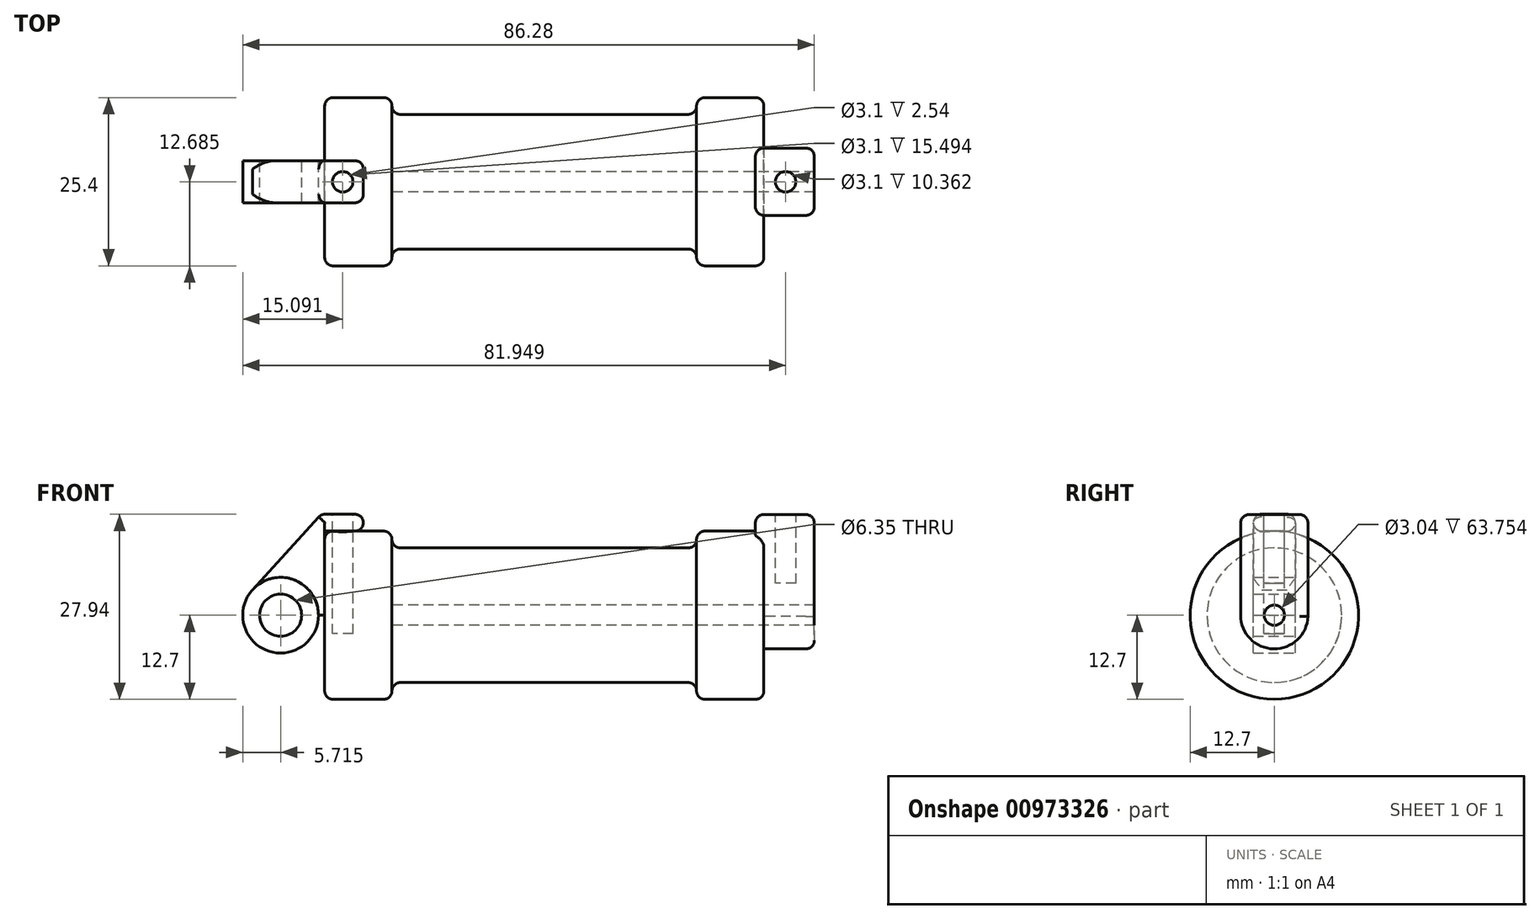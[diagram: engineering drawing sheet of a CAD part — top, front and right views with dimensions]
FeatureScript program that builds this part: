
annotation { "Feature Type Name" : "Feature", "Feature Type Description" : "" }
export const myFeature = defineFeature(function(context is Context, id is Id, definition is map)
    precondition{}
    {
        {
            var Q0;
            Q0=qCreatedBy(makeId("Front.planeOp"),FACE);
            var sketch = newSketch(context, id + "F0", { "sketchPlane" : qUnion([Q0])});
            skLineSegment(sketch, "E0", {"start": v(0, 0) * mm, "end": v(0, 12.7) * mm});
            skLineSegment(sketch, "E1", {"start": v(0, 12.7) * mm, "end": v(10.16, 12.7) * mm});
            skLineSegment(sketch, "E2", {"start": v(10.16, 12.7) * mm, "end": v(10.16, 10.16) * mm});
            skLineSegment(sketch, "E3", {"start": v(10.16, 10.16) * mm, "end": v(56.13, 10.16) * mm});
            skLineSegment(sketch, "E4", {"start": v(56.13, 10.16) * mm, "end": v(56.13, 12.7) * mm});
            skLineSegment(sketch, "E5", {"start": v(56.13, 12.7) * mm, "end": v(66.3, 12.7) * mm});
            skLineSegment(sketch, "E6", {"start": v(66.3, 12.7) * mm, "end": v(66.3, 0) * mm});
            skLineSegment(sketch, "E7", {"start": v(66.3, 0) * mm, "end": v(0, 0) * mm});
            skLineSegment(sketch, "E8", {"start": v(5.84, 15.24) * mm, "end": v(-0.5, 15.24) * mm});
            skLineSegment(sketch, "E9", {"start": v(-0.5, 15.24) * mm, "end": v(-10.88, 3.85) * mm});
            skLineSegment(sketch, "E10", {"start": v(0, 0) * mm, "end": v(-6.65, 0) * mm});
            skCircle(sketch, "E11", {"center": v(-6.65, 0) * mm, "radius": 5.72 * mm});
            skCircle(sketch, "E12", {"center": v(-6.65, 0) * mm, "radius": 3.18 * mm});
            skLineSegment(sketch, "E13", {"start": v(5.84, 15.24) * mm, "end": v(5.84, -9.4) * mm});
            skLineSegment(sketch, "E14", {"start": v(5.84, -9.4) * mm, "end": v(-8.18, -5.5) * mm});
            skSolve(sketch);
        }
        {
            var Q0;
            {var subQ0=sQuery(id+"F0.wireOp",EDGE,"E0");Q0=makeQuery(id+"F0.imprint","IMPRINT",FACE,{"disambiguationData":[TD([[makeQuery(id+"F0.imprint","IMPRINT",EDGE,{"derivedFrom":subQ0}),-1.0]])]});}
            var Q1;
            {var subQ0=sQuery(id+"F0.wireOp",EDGE,"E2");Q1=makeQuery(id+"F0.imprint","IMPRINT",FACE,{"disambiguationData":[TD([[makeQuery(id+"F0.imprint","IMPRINT",EDGE,{"derivedFrom":subQ0}),-1.0]])]});}
            var Q2;
            Q2=sQuery(id+"F0.wireOp",EDGE,"E10");
            revolve(context, id + "F1", {"surfaceOperationType" : NewSurfaceOperationType.NEW, "entities" : qUnion([Q0, Q1]), "axis" : qUnion([Q2]), "revolveType" : RevolveType.FULL});
        }
        {
            var Q0;
            {var subQ5=sQuery(id+"F0.wireOp",EDGE,"E12");Q0=makeQuery(id+"F0.imprint","IMPRINT",FACE,{"disambiguationData":[TD([[makeQuery(id+"F0.imprint","IMPRINT",EDGE,{"derivedFrom":subQ5}),-1.0]])]});}
            extrude(context, id + "F2", {"entities" : qUnion([Q0]), "endBound" : BoundingType.SYMMETRIC, "depth" : 6.35 * mm, "offsetDistance" : 25.4 * mm});
        }
        {
            var Q0;
            {var subQ1=sQuery(id+"F0.wireOp",EDGE,"E0");Q0=makeQuery(id+"F0.imprint","IMPRINT",FACE,{"disambiguationData":[TD([[makeQuery(id+"F0.imprint","IMPRINT",EDGE,{"derivedFrom":subQ1}),1.0]])]});}
            extrude(context, id + "F3", {"entities" : qUnion([Q0]), "endBound" : BoundingType.SYMMETRIC, "depth" : 6.35 * mm, "offsetDistance" : 25.4 * mm});
        }
        {
            var Q0;
            Q0=makeQuery(id+"F1.opRevolve","SWEPT_FACE",FACE,{"disambiguationData":[OSD([sQuery(id+"F0.wireOp",EDGE,"E6")])]});
            var sketch = newSketch(context, id + "F4", { "sketchPlane" : qUnion([Q0])});
            skCircle(sketch, "E15", {"center": v(0, 0) * mm, "radius": 1.52 * mm});
            skCircle(sketch, "E16", {"center": v(0, 0) * mm, "radius": 5.08 * mm});
            skLineSegment(sketch, "E17", {"start": v(-5.08, -0.02) * mm, "end": v(-5.08, 15.19) * mm});
            skLineSegment(sketch, "E18", {"start": v(-5.08, 15.19) * mm, "end": v(5.08, 15.19) * mm});
            skLineSegment(sketch, "E19", {"start": v(5.08, 15.19) * mm, "end": v(5.08, -0.19) * mm});
            skSolve(sketch);
        }
        {
            var Q0;
            {var subQ0=sQuery(id+"F4.wireOp",EDGE,"E17");var subQ1=sQuery(id+"F4.wireOp",EDGE,"E16");var subQ2=makeQuery(id+"F4.imprint","INTERSECT",VERTEX,{"derivedFrom":[subQ1,subQ0]});Q0=makeQuery(id+"F4.imprint","IMPRINT",FACE,{"disambiguationData":[TD([[makeQuery(id+"F4.imprint","IMPRINT",EDGE,{"disambiguationData":[TD([[subQ2,1.0]])],"derivedFrom":subQ1}),-1.0]])]});}
            var Q1;
            Q1=makeQuery(id+"F4.imprint","IMPRINT",FACE,{"disambiguationData":[TD([[makeQuery(id+"F4.imprint","IMPRINT",EDGE,{"derivedFrom":sQuery(id+"F4.wireOp",EDGE,"E15")}),-1.0]])]});
            var Q2;
            {var subQ0=sQuery(id+"F4.wireOp",EDGE,"E18");Q2=makeQuery(id+"F4.imprint","IMPRINT",FACE,{"disambiguationData":[TD([[makeQuery(id+"F4.imprint","IMPRINT",EDGE,{"derivedFrom":subQ0}),-1.0]])]});}
            extrude(context, id + "F5", {"entities" : qUnion([Q0, Q1, Q2]), "operationType" : NewBodyOperationType.ADD, "depth" : 7.62 * mm, "offsetDistance" : 25.4 * mm});
        }
        {
            var Q0;
            Q0 = qSketchRegion(id + "F4", true);
            extrude(context, id + "F6", {"entities" : qUnion([Q0]), "operationType" : NewBodyOperationType.ADD, "oppositeDirection" : true, "depth" : 1.27 * mm, "offsetDistance" : 25.4 * mm});
        }
        {
            var Q0;
            Q0=makeQuery(id+"F5.boolean.opBoolean","SPLIT",FACE,{"disambiguationData":[TD([makeQuery(id+"F5.opExtrude","SWEPT_FACE",FACE,{"disambiguationData":[OSD([sQuery(id+"F4.wireOp",EDGE,"E15")])]})])],"derivedFrom":makeQuery(id+"F1.opRevolve","SWEPT_FACE",FACE,{"disambiguationData":[OSD([sQuery(id+"F0.wireOp",EDGE,"E6")])]})});
            var Q1;
            Q1=makeQuery(id+"F1.opRevolve","SWEPT_FACE",FACE,{"disambiguationData":[OSD([sQuery(id+"F0.wireOp",EDGE,"E2")])]});
            var Q2;
            Q2=makeQuery(id+"F1.opRevolve","SWEPT_BODY",BODY,{"disambiguationData":[OSD([sQuery(id+"F0.wireOp",EDGE,"E0"),sQuery(id+"F0.wireOp",EDGE,"E1"),sQuery(id+"F0.wireOp",EDGE,"E2"),sQuery(id+"F0.wireOp",EDGE,"E3"),sQuery(id+"F0.wireOp",EDGE,"E4"),sQuery(id+"F0.wireOp",EDGE,"E5"),sQuery(id+"F0.wireOp",EDGE,"E6"),sQuery(id+"F0.wireOp",EDGE,"E7")])]});
            extrude(context, id + "F7", {"entities" : qUnion([Q0]), "operationType" : NewBodyOperationType.ADD, "oppositeDirection" : true, "depth" : 60.32 * mm, "endBoundEntityFace" : qUnion([Q1]), "endBoundEntityBody" : qUnion([Q2]), "offsetDistance" : 25.4 * mm});
        }
        {
            var Q0;
            Q0=makeQuery(id+"F5.boolean.opBoolean","SPLIT",FACE,{"disambiguationData":[TD([makeQuery(id+"F5.opExtrude","SWEPT_FACE",FACE,{"disambiguationData":[OSD([sQuery(id+"F4.wireOp",EDGE,"E15")])]})])],"derivedFrom":makeQuery(id+"F1.opRevolve","SWEPT_FACE",FACE,{"disambiguationData":[OSD([sQuery(id+"F0.wireOp",EDGE,"E6")])]})});
            extrude(context, id + "F8", {"entities" : qUnion([Q0]), "operationType" : NewBodyOperationType.REMOVE, "oppositeDirection" : true, "depth" : 56.13 * mm, "offsetDistance" : 25.4 * mm});
        }
        {
            var Q0;
            Q0=makeQuery(id+"F3.opExtrude","SWEPT_FACE",FACE,{"disambiguationData":[OSD([sQuery(id+"F0.wireOp",EDGE,"E8")])]});
            var sketch = newSketch(context, id + "F9", { "sketchPlane" : qUnion([Q0])});
            skCircle(sketch, "E20", {"center": v(2.72, -0.01) * mm, "radius": 1.55 * mm});
            skCircle(sketch, "E21", {"center": v(69.58, -0.01) * mm, "radius": 1.55 * mm});
            skSolve(sketch);
        }
        {
            var Q0;
            Q0=makeQuery(id+"F9.imprint","IMPRINT",FACE,{"disambiguationData":[TD([[makeQuery(id+"F9.imprint","IMPRINT",EDGE,{"derivedFrom":sQuery(id+"F9.wireOp",EDGE,"E20")}),1.0]])]});
            var Q1;
            Q1=sQuery(id+"F9.wireOp",EDGE,"E20");
            extrude(context, id + "F10", {"entities" : qUnion([Q0]), "operationType" : NewBodyOperationType.REMOVE, "surfaceEntities" : qUnion([Q1]), "oppositeDirection" : true, "depth" : 18.03 * mm, "offsetDistance" : 25.4 * mm});
        }
        {
            var Q0;
            Q0=makeQuery(id+"F9.imprint","IMPRINT",FACE,{"disambiguationData":[TD([[makeQuery(id+"F9.imprint","IMPRINT",EDGE,{"derivedFrom":sQuery(id+"F9.wireOp",EDGE,"E21")}),1.0]])]});
            extrude(context, id + "F11", {"entities" : qUnion([Q0]), "operationType" : NewBodyOperationType.REMOVE, "oppositeDirection" : true, "depth" : 10.4 * mm, "offsetDistance" : 25.4 * mm});
        }
        {
            var Q0;
            Q0=makeQuery(id+"F1.opRevolve","SWEPT_EDGE",EDGE,{"disambiguationData":[OSD([sQuery(id+"F0.wireOp",EDGE,"E1"),sQuery(id+"F0.wireOp",EDGE,"E2")])]});
            var Q1;
            Q1=makeQuery(id+"F1.opRevolve","SWEPT_EDGE",EDGE,{"disambiguationData":[OSD([sQuery(id+"F0.wireOp",EDGE,"E0"),sQuery(id+"F0.wireOp",EDGE,"E1")])]});
            var Q2;
            Q2=makeQuery(id+"F1.opRevolve","SWEPT_EDGE",EDGE,{"disambiguationData":[OSD([sQuery(id+"F0.wireOp",EDGE,"E4"),sQuery(id+"F0.wireOp",EDGE,"E5")])]});
            var Q3;
            {var subQ0=sQuery(id+"F0.wireOp",EDGE,"E5");var subQ1=sQuery(id+"F0.wireOp",EDGE,"E6");Q3=makeQuery(id+"F5.boolean.opBoolean","SPLIT",EDGE,{"disambiguationData":[topologyDisambiguationEdgeConnected([makeQuery(id+"F1.opRevolve","SWEPT_FACE",FACE,{"disambiguationData":[OSD([subQ1])]})])],"derivedFrom":makeQuery(id+"F1.opRevolve","SWEPT_EDGE",EDGE,{"disambiguationData":[OSD([subQ0,subQ1])]})});}
            fillet(context, id + "F12", {"entities" : qUnion([Q0, Q1, Q2, Q3]), "radius" : 1.27 * mm, "tangentPropagation" : true, "allowEdgeOverflow" : false});
        }
        {
            var Q0;
            Q0=makeQuery(id+"F1.opRevolve","SWEPT_EDGE",EDGE,{"disambiguationData":[OSD([sQuery(id+"F0.wireOp",EDGE,"E2"),sQuery(id+"F0.wireOp",EDGE,"E3")])]});
            var Q1;
            Q1=makeQuery(id+"F1.opRevolve","SWEPT_EDGE",EDGE,{"disambiguationData":[OSD([sQuery(id+"F0.wireOp",EDGE,"E3"),sQuery(id+"F0.wireOp",EDGE,"E4")])]});
            fillet(context, id + "F13", {"entities" : qUnion([Q0, Q1]), "radius" : 1.27 * mm, "tangentPropagation" : true, "allowEdgeOverflow" : false});
        }
        {
            var Q0;
            Q0=makeQuery(id+"F3.opExtrude","CAP_EDGE",EDGE,{"disambiguationData":[OSD([sQuery(id+"F0.wireOp",EDGE,"E9")])],"isStart":false});
            var Q1;
            Q1=makeQuery(id+"F3.opExtrude","CAP_EDGE",EDGE,{"disambiguationData":[OSD([sQuery(id+"F0.wireOp",EDGE,"E9")])],"isStart":true});
            fillet(context, id + "F14", {"entities" : qUnion([Q0, Q1]), "radius" : 1.27 * mm, "tangentPropagation" : true, "allowEdgeOverflow" : false});
        }
        {
            var Q0;
            Q0=makeQuery(id+"F3.opExtrude","CAP_EDGE",EDGE,{"disambiguationData":[OSD([sQuery(id+"F0.wireOp",EDGE,"E8")])],"isStart":false});
            var Q1;
            Q1=makeQuery(id+"F3.opExtrude","SWEPT_EDGE",EDGE,{"disambiguationData":[OSD([sQuery(id+"F0.wireOp",EDGE,"E8"),sQuery(id+"F0.wireOp",EDGE,"E13")])]});
            var Q2;
            Q2=makeQuery(id+"F3.opExtrude","CAP_EDGE",EDGE,{"disambiguationData":[OSD([sQuery(id+"F0.wireOp",EDGE,"E1")])],"isStart":true});
            var Q3;
            Q3=makeQuery(id+"F3.opExtrude","SWEPT_EDGE",EDGE,{"disambiguationData":[OSD([sQuery(id+"F0.wireOp",EDGE,"E1"),sQuery(id+"F0.wireOp",EDGE,"E13")])]});
            var Q4;
            Q4=makeQuery(id+"F3.opExtrude","CAP_EDGE",EDGE,{"disambiguationData":[OSD([sQuery(id+"F0.wireOp",EDGE,"E13")])],"isStart":true});
            var Q5;
            Q5=makeQuery(id+"F3.opExtrude","CAP_EDGE",EDGE,{"disambiguationData":[OSD([sQuery(id+"F0.wireOp",EDGE,"E13")])],"isStart":false});
            var Q6;
            Q6=makeQuery(id+"F3.opExtrude","CAP_EDGE",EDGE,{"disambiguationData":[OSD([sQuery(id+"F0.wireOp",EDGE,"E1")])],"isStart":false});
            fillet(context, id + "F15", {"entities" : qUnion([Q0, Q1, Q2, Q3, Q4, Q5, Q6]), "radius" : 1.27 * mm, "tangentPropagation" : true, "allowEdgeOverflow" : false});
        }
        {
            var Q0;
            Q0=makeQuery(id+"F5.opExtrude","CAP_EDGE",EDGE,{"disambiguationData":[OSD([sQuery(id+"F4.wireOp",EDGE,"E17")])],"isStart":false});
            var Q1;
            Q1=makeQuery(id+"F5.opExtrude","CAP_EDGE",EDGE,{"disambiguationData":[OSD([sQuery(id+"F4.wireOp",EDGE,"E16")])],"isStart":false});
            var Q2;
            Q2=makeQuery(id+"F5.opExtrude","CAP_EDGE",EDGE,{"disambiguationData":[OSD([sQuery(id+"F4.wireOp",EDGE,"E19")])],"isStart":false});
            var Q3;
            Q3=makeQuery(id+"F5.opExtrude","CAP_EDGE",EDGE,{"disambiguationData":[OSD([sQuery(id+"F4.wireOp",EDGE,"E18")])],"isStart":false});
            var Q4;
            {var subQ0=sQuery(id+"F4.wireOp",EDGE,"E19");var subQ1=sQuery(id+"F4.wireOp",EDGE,"E18");Q4=makeQuery(id+"F6.boolean.opBoolean","MERGE",EDGE,{"derivedFrom":[makeQuery(id+"F5.opExtrude","SWEPT_EDGE",EDGE,{"disambiguationData":[OSD([subQ1,subQ0])]}),makeQuery(id+"F6.opExtrude","SWEPT_EDGE",EDGE,{"disambiguationData":[OSD([subQ1,subQ0])]})]});}
            var Q5;
            {var subQ0=sQuery(id+"F4.wireOp",EDGE,"E18");var subQ1=sQuery(id+"F4.wireOp",EDGE,"E17");Q5=makeQuery(id+"F6.boolean.opBoolean","MERGE",EDGE,{"derivedFrom":[makeQuery(id+"F5.opExtrude","SWEPT_EDGE",EDGE,{"disambiguationData":[OSD([subQ1,subQ0])]}),makeQuery(id+"F6.opExtrude","SWEPT_EDGE",EDGE,{"disambiguationData":[OSD([subQ1,subQ0])]})]});}
            var Q6;
            Q6=makeQuery(id+"F6.opExtrude","CAP_EDGE",EDGE,{"disambiguationData":[OSD([sQuery(id+"F4.wireOp",EDGE,"E18")])],"isStart":false});
            fillet(context, id + "F16", {"entities" : qUnion([Q0, Q1, Q2, Q3, Q4, Q5, Q6]), "radius" : 1.27 * mm, "tangentPropagation" : true, "allowEdgeOverflow" : false});
        }
        {
            var Q0;
            Q0=makeQuery(id+"F6.opExtrude","CAP_EDGE",EDGE,{"disambiguationData":[OSD([sQuery(id+"F4.wireOp",EDGE,"E17")])],"isStart":false});
            var Q1;
            Q1=makeQuery(id+"F6.opExtrude","CAP_EDGE",EDGE,{"disambiguationData":[OSD([sQuery(id+"F4.wireOp",EDGE,"E19")])],"isStart":false});
            fillet(context, id + "F17", {"entities" : qUnion([Q0, Q1]), "radius" : 1.27 * mm, "tangentPropagation" : true, "allowEdgeOverflow" : false});
        }
    });
